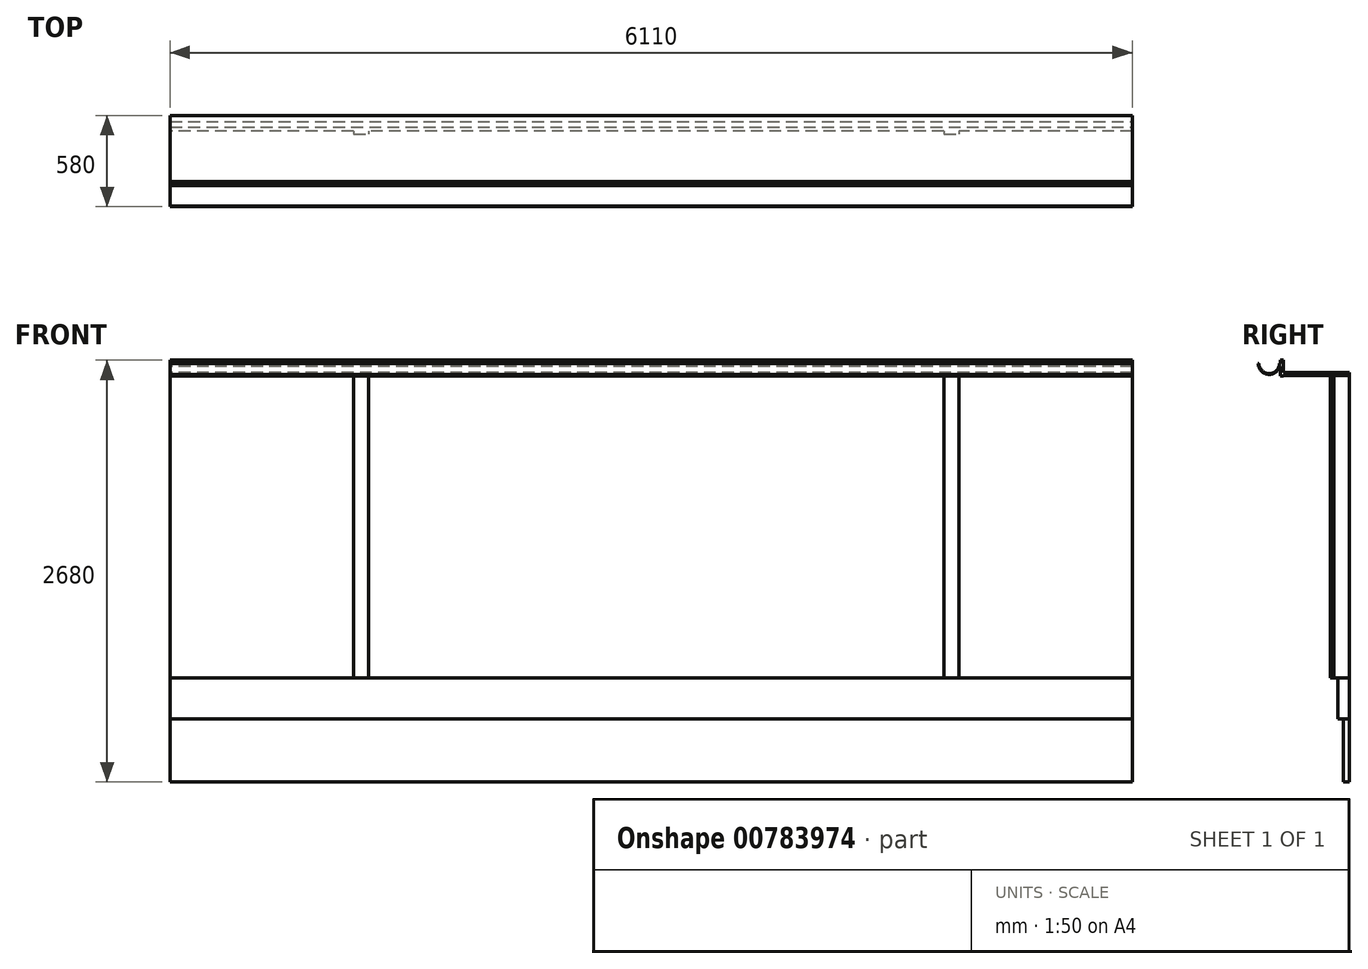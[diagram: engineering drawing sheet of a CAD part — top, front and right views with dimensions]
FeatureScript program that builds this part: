
annotation { "Feature Type Name" : "Feature", "Feature Type Description" : "" }
export const myFeature = defineFeature(function(context is Context, id is Id, definition is map)
    precondition{}
    {
        {
            var Q0;
            Q0=qCreatedBy(makeId("Front.planeOp"),FACE);
            var sketch = newSketch(context, id + "F0", { "sketchPlane" : qUnion([Q0])});
            skLineSegment(sketch, "E0.bottom", {"start": v(0, 0) * mm, "end": v(-6110, 0) * mm});
            skLineSegment(sketch, "E0.top", {"start": v(0, 1920) * mm, "end": v(-6110, 1920) * mm});
            skLineSegment(sketch, "E0.left", {"start": v(0, 0) * mm, "end": v(0, 1920) * mm});
            skLineSegment(sketch, "E0.right", {"start": v(-6110, 0) * mm, "end": v(-6110, 1920) * mm});
            skSolve(sketch);
        }
        {
            var Q0;
            Q0=makeQuery(id+"F0.imprint","IMPRINT",FACE,{"disambiguationData":[TD([[makeQuery(id+"F0.imprint","IMPRINT",EDGE,{"derivedFrom":sQuery(id+"F0.wireOp",EDGE,"E0.bottom")}),-1.0]])]});
            extrude(context, id + "F1", {"entities" : qUnion([Q0]), "depth" : 100 * mm, "offsetDistance" : 25 * mm});
        }
        {
            var Q0;
            Q0=makeQuery(id+"F1.opExtrude","SWEPT_FACE",FACE,{"disambiguationData":[OSD([sQuery(id+"F0.wireOp",EDGE,"E0.bottom")])]});
            var sketch = newSketch(context, id + "F2", { "sketchPlane" : qUnion([Q0])});
            skLineSegment(sketch, "E1.bottom", {"start": v(-4945, 100) * mm, "end": v(-4850, 100) * mm});
            skLineSegment(sketch, "E1.top", {"start": v(-4945, 120) * mm, "end": v(-4850, 120) * mm});
            skLineSegment(sketch, "E1.left", {"start": v(-4945, 100) * mm, "end": v(-4945, 120) * mm});
            skLineSegment(sketch, "E1.right", {"start": v(-4850, 100) * mm, "end": v(-4850, 120) * mm});
            skLineSegment(sketch, "E2.bottom", {"start": v(-1195, 100) * mm, "end": v(-1100, 100) * mm});
            skLineSegment(sketch, "E2.top", {"start": v(-1195, 120) * mm, "end": v(-1100, 120) * mm});
            skLineSegment(sketch, "E2.left", {"start": v(-1195, 100) * mm, "end": v(-1195, 120) * mm});
            skLineSegment(sketch, "E2.right", {"start": v(-1100, 100) * mm, "end": v(-1100, 120) * mm});
            skSolve(sketch);
        }
        {
            var Q0;
            Q0=makeQuery(id+"F2.imprint","IMPRINT",FACE,{"disambiguationData":[TD([[makeQuery(id+"F2.imprint","IMPRINT",EDGE,{"derivedFrom":sQuery(id+"F2.wireOp",EDGE,"E1.bottom")}),-1.0]])]});
            var Q1;
            Q1=makeQuery(id+"F2.imprint","IMPRINT",FACE,{"disambiguationData":[TD([[makeQuery(id+"F2.imprint","IMPRINT",EDGE,{"derivedFrom":sQuery(id+"F2.wireOp",EDGE,"E2.bottom")}),-1.0]])]});
            var Q2;
            Q2=makeQuery(id+"F1.opExtrude","SWEPT_FACE",FACE,{"disambiguationData":[OSD([sQuery(id+"F0.wireOp",EDGE,"E0.top")])]});
            extrude(context, id + "F3", {"entities" : qUnion([Q0, Q1]), "operationType" : NewBodyOperationType.ADD, "endBound" : BoundingType.UP_TO_SURFACE, "oppositeDirection" : true, "depth" : 25 * mm, "endBoundEntityFace" : qUnion([Q2]), "offsetDistance" : 25 * mm});
        }
        {
            var Q0;
            Q0=makeQuery(id+"F1.opExtrude","SWEPT_FACE",FACE,{"disambiguationData":[OSD([sQuery(id+"F0.wireOp",EDGE,"E0.right")])]});
            var sketch = newSketch(context, id + "F4", { "sketchPlane" : qUnion([Q0])});
            skLineSegment(sketch, "E3.bottom", {"start": v(0, 1920) * mm, "end": v(420, 1920) * mm});
            skLineSegment(sketch, "E3.top", {"start": v(0, 1940) * mm, "end": v(420, 1940) * mm});
            skLineSegment(sketch, "E3.left", {"start": v(0, 1920) * mm, "end": v(0, 1940) * mm});
            skLineSegment(sketch, "E3.right", {"start": v(420, 1920) * mm, "end": v(420, 1940) * mm});
            skLineSegment(sketch, "E4.bottom", {"start": v(420, 1917) * mm, "end": v(440, 1917) * mm});
            skLineSegment(sketch, "E4.top", {"start": v(420, 2017) * mm, "end": v(440, 2017) * mm});
            skLineSegment(sketch, "E4.left", {"start": v(420, 1917) * mm, "end": v(420, 2017) * mm});
            skLineSegment(sketch, "E4.right", {"start": v(440, 1917) * mm, "end": v(440, 2017) * mm});
            skLineSegment(sketch, "E5", {"start": v(440, 1997) * mm, "end": v(445, 1997) * mm});
            skArc(sketch, "E6", {"start": v(442.92, 1977) * mm, "mid": v(520.1, 1927.73) * mm, "end": v(580, 1997) * mm});
            skLineSegment(sketch, "E7", {"start": v(580, 1997) * mm, "end": v(575, 1997) * mm});
            skArc(sketch, "E8", {"start": v(445, 1997) * mm, "mid": v(510, 1932) * mm, "end": v(575, 1997) * mm});
            skLineSegment(sketch, "E9", {"start": v(442.92, 1977) * mm, "end": v(440, 1977) * mm});
            skSolve(sketch);
        }
        {
            var Q0;
            {var subQ1=sQuery(id+"F4.wireOp",EDGE,"E3.top");Q0=makeQuery(id+"F4.imprint","IMPRINT",FACE,{"disambiguationData":[TD([[makeQuery(id+"F4.imprint","IMPRINT",EDGE,{"derivedFrom":subQ1}),-1.0]])]});}
            var Q1;
            {var subQ3=sQuery(id+"F4.wireOp",EDGE,"E4.bottom");Q1=makeQuery(id+"F4.imprint","IMPRINT",FACE,{"disambiguationData":[TD([[makeQuery(id+"F4.imprint","IMPRINT",EDGE,{"derivedFrom":subQ3}),1.0]])]});}
            var Q2;
            Q2=makeQuery(id+"F4.imprint","IMPRINT",FACE,{"disambiguationData":[TD([[makeQuery(id+"F4.imprint","IMPRINT",EDGE,{"derivedFrom":sQuery(id+"F4.wireOp",EDGE,"E5")}),-1.0]])]});
            var Q3;
            Q3=makeQuery(id+"F1.opExtrude","SWEPT_FACE",FACE,{"disambiguationData":[OSD([sQuery(id+"F0.wireOp",EDGE,"E0.left")])]});
            extrude(context, id + "F5", {"entities" : qUnion([Q0, Q1, Q2]), "endBound" : BoundingType.UP_TO_SURFACE, "oppositeDirection" : true, "depth" : 25 * mm, "endBoundEntityFace" : qUnion([Q3]), "offsetDistance" : 25 * mm});
        }
        {
            var Q0;
            Q0=makeQuery(id+"F3.boolean.opBoolean","MERGE",FACE,{"derivedFrom":[makeQuery(id+"F1.opExtrude","SWEPT_FACE",FACE,{"disambiguationData":[OSD([sQuery(id+"F0.wireOp",EDGE,"E0.bottom")])]}),makeQuery(id+"F3.opExtrude","CAP_FACE",FACE,{"disambiguationData":[OSD([sQuery(id+"F2.wireOp",EDGE,"E1.bottom"),sQuery(id+"F2.wireOp",EDGE,"E1.top"),sQuery(id+"F2.wireOp",EDGE,"E1.left"),sQuery(id+"F2.wireOp",EDGE,"E1.right")])],"isStart":true}),makeQuery(id+"F3.opExtrude","CAP_FACE",FACE,{"disambiguationData":[OSD([sQuery(id+"F2.wireOp",EDGE,"E2.bottom"),sQuery(id+"F2.wireOp",EDGE,"E2.top"),sQuery(id+"F2.wireOp",EDGE,"E2.left"),sQuery(id+"F2.wireOp",EDGE,"E2.right")])],"isStart":true})]});
            var sketch = newSketch(context, id + "F6", { "sketchPlane" : qUnion([Q0])});
            skLineSegment(sketch, "E10.bottom", {"start": v(-6110, 0) * mm, "end": v(0, 0) * mm});
            skLineSegment(sketch, "E10.top", {"start": v(-6110, 75) * mm, "end": v(0, 75) * mm});
            skLineSegment(sketch, "E10.left", {"start": v(-6110, 0) * mm, "end": v(-6110, 75) * mm});
            skLineSegment(sketch, "E10.right", {"start": v(0, 0) * mm, "end": v(0, 75) * mm});
            skSolve(sketch);
        }
        {
            var Q0;
            Q0=makeQuery(id+"F6.imprint","IMPRINT",FACE,{"disambiguationData":[TD([[makeQuery(id+"F6.imprint","IMPRINT",EDGE,{"derivedFrom":sQuery(id+"F6.wireOp",EDGE,"E10.bottom")}),-1.0]])]});
            extrude(context, id + "F7", {"entities" : qUnion([Q0]), "depth" : 263 * mm, "offsetDistance" : 25 * mm});
        }
        {
            var Q0;
            Q0=makeQuery(id+"F7.opExtrude","CAP_FACE",FACE,{"disambiguationData":[OSD([sQuery(id+"F6.wireOp",EDGE,"E10.bottom"),sQuery(id+"F6.wireOp",EDGE,"E10.top"),sQuery(id+"F6.wireOp",EDGE,"E10.left"),sQuery(id+"F6.wireOp",EDGE,"E10.right")])],"isStart":false});
            var sketch = newSketch(context, id + "F8", { "sketchPlane" : qUnion([Q0])});
            skLineSegment(sketch, "E11.bottom", {"start": v(-6110, 0) * mm, "end": v(0, 0) * mm});
            skLineSegment(sketch, "E11.top", {"start": v(-6110, 40) * mm, "end": v(0, 40) * mm});
            skLineSegment(sketch, "E11.left", {"start": v(-6110, 0) * mm, "end": v(-6110, 40) * mm});
            skLineSegment(sketch, "E11.right", {"start": v(0, 0) * mm, "end": v(0, 40) * mm});
            skSolve(sketch);
        }
        {
            var Q0;
            Q0=makeQuery(id+"F8.imprint","IMPRINT",FACE,{"disambiguationData":[TD([[makeQuery(id+"F8.imprint","IMPRINT",EDGE,{"derivedFrom":sQuery(id+"F8.wireOp",EDGE,"E11.bottom")}),-1.0]])]});
            extrude(context, id + "F9", {"entities" : qUnion([Q0]), "depth" : 400 * mm, "offsetDistance" : 25 * mm});
        }
    });
